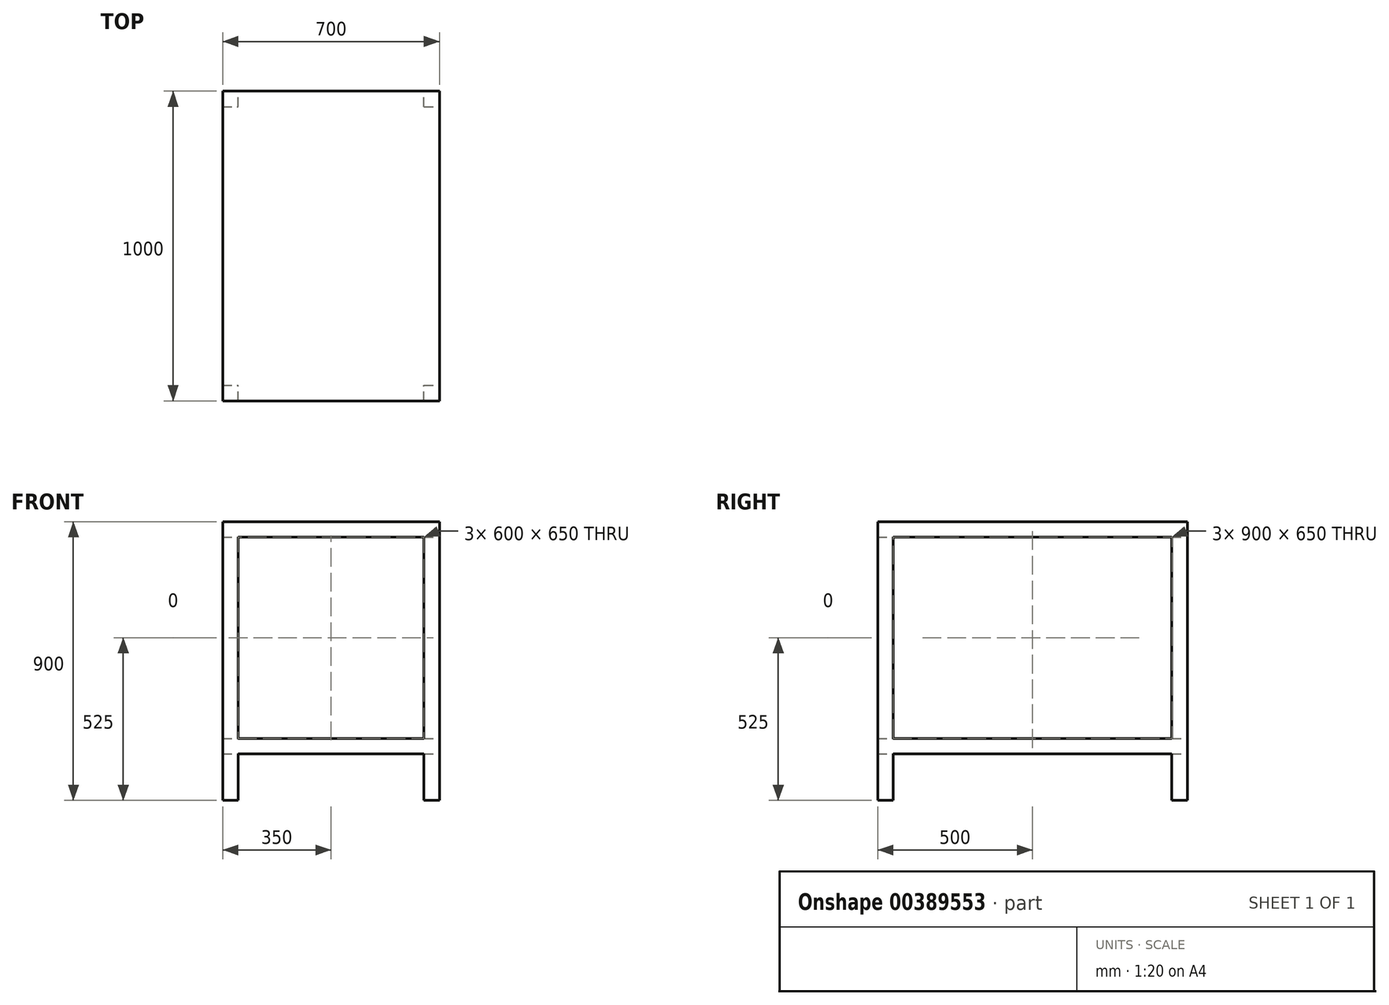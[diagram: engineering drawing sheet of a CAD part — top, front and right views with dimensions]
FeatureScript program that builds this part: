
annotation { "Feature Type Name" : "Feature", "Feature Type Description" : "" }
export const myFeature = defineFeature(function(context is Context, id is Id, definition is map)
    precondition{}
    {
        {
            var Q0;
            Q0=qCreatedBy(makeId("Top.planeOp"),FACE);
            var sketch = newSketch(context, id + "F0", { "sketchPlane" : qUnion([Q0])});
            skLineSegment(sketch, "E0.bottom", {"start": v(350, 500) * mm, "end": v(-350, 500) * mm});
            skLineSegment(sketch, "E0.top", {"start": v(350, -500) * mm, "end": v(-350, -500) * mm});
            skLineSegment(sketch, "E0.left", {"start": v(350, 500) * mm, "end": v(350, -500) * mm});
            skLineSegment(sketch, "E0.right", {"start": v(-350, 500) * mm, "end": v(-350, -500) * mm});
            skPoint(sketch, "E0.middle", {"position": v(0, 0) * mm});
            skSolve(sketch);
        }
        {
            var Q0;
            Q0=makeQuery(id+"F0.imprint","IMPRINT",FACE,{"disambiguationData":[TD([[makeQuery(id+"F0.imprint","IMPRINT",EDGE,{"derivedFrom":sQuery(id+"F0.wireOp",EDGE,"E0.bottom")}),1.0]])]});
            extrude(context, id + "F1", {"entities" : qUnion([Q0]), "depth" : 900 * mm});
        }
        {
            var Q0;
            Q0=makeQuery(id+"F1.opExtrude","SWEPT_FACE",FACE,{"disambiguationData":[OSD([sQuery(id+"F0.wireOp",EDGE,"E0.left")])]});
            var sketch = newSketch(context, id + "F2", { "sketchPlane" : qUnion([Q0])});
            skLineSegment(sketch, "E1.0.0", {"start": v(-500, 0) * mm, "end": v(500, 0) * mm});
            skLineSegment(sketch, "E1.0.1", {"start": v(500, 0) * mm, "end": v(500, 900) * mm});
            skLineSegment(sketch, "E1.0.2", {"start": v(400, 900) * mm, "end": v(-500, 900) * mm});
            skLineSegment(sketch, "E1.0.3", {"start": v(-500, 900) * mm, "end": v(-500, 0) * mm});
            skLineSegment(sketch, "E2.bottom", {"start": v(-450, 850) * mm, "end": v(450, 850) * mm});
            skLineSegment(sketch, "E2.top", {"start": v(-450, 200) * mm, "end": v(450, 200) * mm});
            skLineSegment(sketch, "E2.left", {"start": v(-450, 850) * mm, "end": v(-450, 200) * mm});
            skLineSegment(sketch, "E2.right", {"start": v(450, 850) * mm, "end": v(450, 200) * mm});
            skLineSegment(sketch, "E3.bottom", {"start": v(-450, 150) * mm, "end": v(450, 150) * mm});
            skLineSegment(sketch, "E3.top", {"start": v(-450, -97.38) * mm, "end": v(450, -97.38) * mm});
            skLineSegment(sketch, "E3.left", {"start": v(-450, 150) * mm, "end": v(-450, -97.38) * mm});
            skLineSegment(sketch, "E3.right", {"start": v(450, 150) * mm, "end": v(450, -97.38) * mm});
            skSolve(sketch);
        }
        {
            var Q0;
            {var subQ5=sQuery(id+"F2.wireOp",EDGE,"E3.top");Q0=makeQuery(id+"F2.imprint","IMPRINT",FACE,{"disambiguationData":[TD([[makeQuery(id+"F2.imprint","IMPRINT",EDGE,{"derivedFrom":subQ5}),1.0]])]});}
            var Q1;
            {var subQ5=sQuery(id+"F2.wireOp",EDGE,"E3.bottom");Q1=makeQuery(id+"F2.imprint","IMPRINT",FACE,{"disambiguationData":[TD([[makeQuery(id+"F2.imprint","IMPRINT",EDGE,{"derivedFrom":subQ5}),-1.0]])]});}
            var Q2;
            Q2=makeQuery(id+"F2.imprint","IMPRINT",FACE,{"disambiguationData":[TD([[makeQuery(id+"F2.imprint","IMPRINT",EDGE,{"derivedFrom":sQuery(id+"F2.wireOp",EDGE,"E2.bottom")}),-1.0]])]});
            extrude(context, id + "F3", {"entities" : qUnion([Q0, Q1, Q2]), "operationType" : NewBodyOperationType.REMOVE, "oppositeDirection" : true, "depth" : 1000 * mm});
        }
        {
            var Q0;
            Q0=makeQuery(id+"F1.opExtrude","SWEPT_FACE",FACE,{"disambiguationData":[OSD([sQuery(id+"F0.wireOp",EDGE,"E0.bottom")])]});
            var sketch = newSketch(context, id + "F4", { "sketchPlane" : qUnion([Q0])});
            skLineSegment(sketch, "E4.bottom", {"start": v(-300, 850) * mm, "end": v(300, 850) * mm});
            skLineSegment(sketch, "E4.top", {"start": v(-300, 200) * mm, "end": v(300, 200) * mm});
            skLineSegment(sketch, "E4.left", {"start": v(-300, 850) * mm, "end": v(-300, 200) * mm});
            skLineSegment(sketch, "E4.right", {"start": v(300, 850) * mm, "end": v(300, 200) * mm});
            skLineSegment(sketch, "E5.bottom", {"start": v(300, 150) * mm, "end": v(-300, 150) * mm});
            skLineSegment(sketch, "E5.top", {"start": v(300, -174.41) * mm, "end": v(-300, -174.41) * mm});
            skLineSegment(sketch, "E5.left", {"start": v(300, 150) * mm, "end": v(300, -174.41) * mm});
            skLineSegment(sketch, "E5.right", {"start": v(-300, 150) * mm, "end": v(-300, -174.41) * mm});
            skSolve(sketch);
        }
        {
            var Q0;
            {var subQ0=sQuery(id+"F4.wireOp",EDGE,"E5.top");Q0=makeQuery(id+"F4.imprint","IMPRINT",FACE,{"disambiguationData":[TD([[makeQuery(id+"F4.imprint","IMPRINT",EDGE,{"derivedFrom":subQ0}),-1.0]])]});}
            var Q1;
            {var subQ0=sQuery(id+"F4.wireOp",EDGE,"E5.bottom");Q1=makeQuery(id+"F4.imprint","IMPRINT",FACE,{"disambiguationData":[TD([[makeQuery(id+"F4.imprint","IMPRINT",EDGE,{"derivedFrom":subQ0}),1.0]])]});}
            var Q2;
            Q2=makeQuery(id+"F4.imprint","IMPRINT",FACE,{"disambiguationData":[TD([[makeQuery(id+"F4.imprint","IMPRINT",EDGE,{"derivedFrom":sQuery(id+"F4.wireOp",EDGE,"E4.bottom")}),-1.0]])]});
            extrude(context, id + "F5", {"entities" : qUnion([Q0, Q1, Q2]), "operationType" : NewBodyOperationType.REMOVE, "oppositeDirection" : true, "depth" : 1000 * mm});
        }
    });
